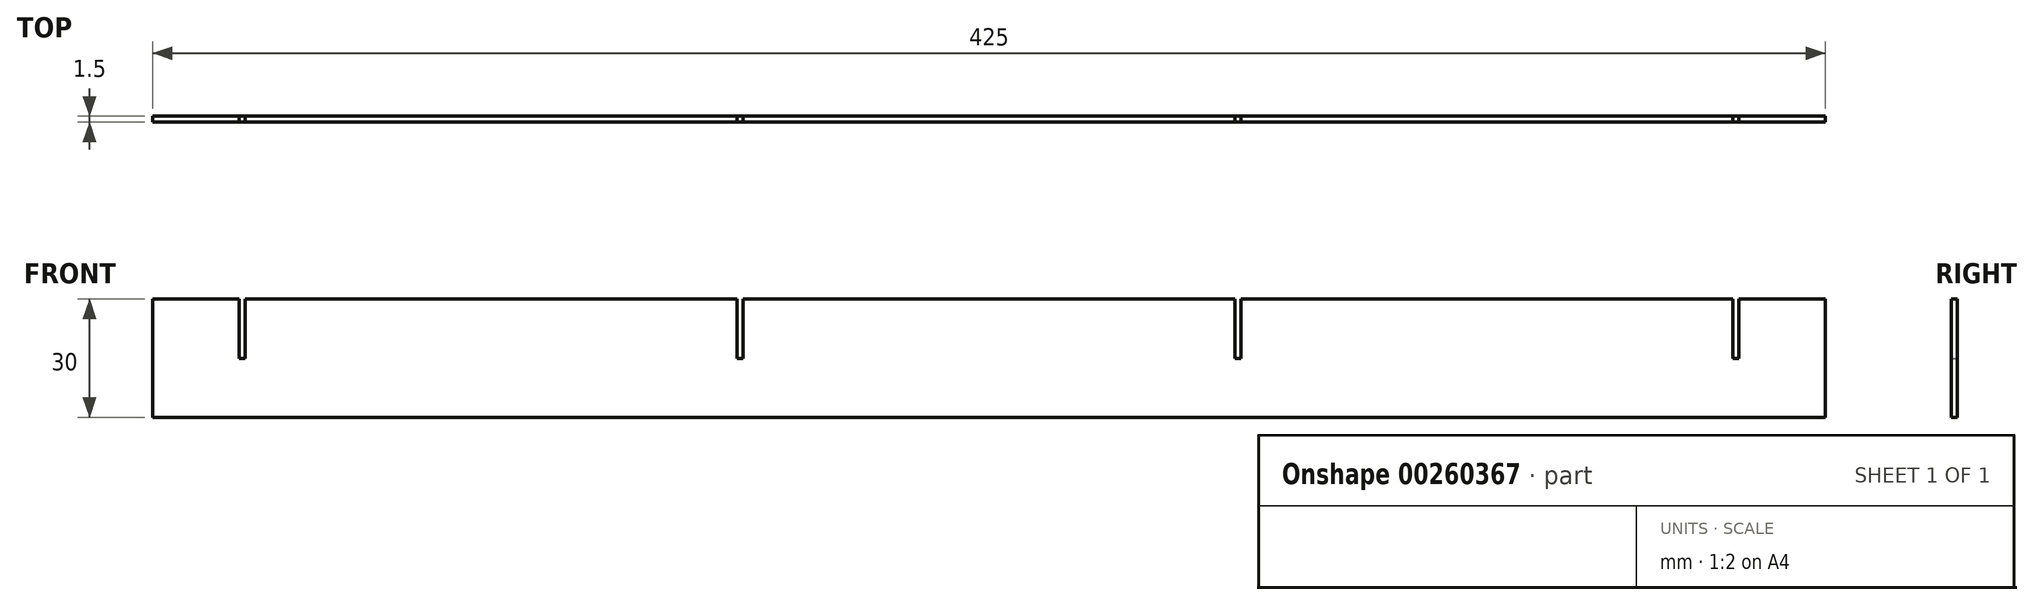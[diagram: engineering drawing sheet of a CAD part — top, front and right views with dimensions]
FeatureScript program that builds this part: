
annotation { "Feature Type Name" : "Feature", "Feature Type Description" : "" }
export const myFeature = defineFeature(function(context is Context, id is Id, definition is map)
    precondition{}
    {
        {
            var Q0;
            Q0=qCreatedBy(makeId("Front.planeOp"),FACE);
            var sketch = newSketch(context, id + "F0", { "sketchPlane" : qUnion([Q0])});
            skLineSegment(sketch, "E0.bottom", {"start": v(212.5, 15) * mm, "end": v(190.5, 15) * mm});
            skLineSegment(sketch, "E0.top", {"start": v(212.5, -15) * mm, "end": v(-212.5, -15) * mm});
            skLineSegment(sketch, "E0.left", {"start": v(212.5, 15) * mm, "end": v(212.5, -15) * mm});
            skLineSegment(sketch, "E0.right", {"start": v(-212.5, 15) * mm, "end": v(-212.5, -15) * mm});
            skPoint(sketch, "E0.middle", {"position": v(0, 0) * mm});
            skLineSegment(sketch, "E1", {"start": v(-190.5, 15) * mm, "end": v(-190.5, 0) * mm});
            skLineSegment(sketch, "E2", {"start": v(-190.5, 0) * mm, "end": v(-189, 0) * mm});
            skLineSegment(sketch, "E3", {"start": v(-189, 0) * mm, "end": v(-189, 15) * mm});
            skLineSegment(sketch, "E4", {"start": v(-64, 15) * mm, "end": v(-64, 0) * mm});
            skLineSegment(sketch, "E5", {"start": v(-64, 0) * mm, "end": v(-62.5, 0) * mm});
            skLineSegment(sketch, "E6", {"start": v(-62.5, 0) * mm, "end": v(-62.5, 15) * mm});
            skLineSegment(sketch, "E7.MirrorCS", {"start": v(190.5, 0) * mm, "end": v(189, 0) * mm});
            skLineSegment(sketch, "E8.MirrorCS", {"start": v(64, 0) * mm, "end": v(62.5, 0) * mm});
            skLineSegment(sketch, "E9.MirrorCS", {"start": v(62.5, 0) * mm, "end": v(62.5, 15) * mm});
            skLineSegment(sketch, "E10.MirrorCS", {"start": v(64, 15) * mm, "end": v(64, 0) * mm});
            skLineSegment(sketch, "E11.MirrorCS", {"start": v(-212.5, 15) * mm, "end": v(-190.5, 15) * mm});
            skLineSegment(sketch, "E12.MirrorCS", {"start": v(190.5, 15) * mm, "end": v(190.5, 0) * mm});
            skLineSegment(sketch, "E13.MirrorCS", {"start": v(189, 0) * mm, "end": v(189, 15) * mm});
            skLineSegment(sketch, "E14.trimOffspring", {"start": v(-190.5, 15) * mm, "end": v(-212.5, 15) * mm});
            skLineSegment(sketch, "E15.trimOffspring", {"start": v(-189, 15) * mm, "end": v(-64, 15) * mm});
            skLineSegment(sketch, "E16.trimOffspring", {"start": v(-62.5, 15) * mm, "end": v(62.5, 15) * mm});
            skLineSegment(sketch, "E17.trimOffspring", {"start": v(-64, 15) * mm, "end": v(-189, 15) * mm});
            skLineSegment(sketch, "E18.trimOffspring", {"start": v(62.5, 15) * mm, "end": v(-62.5, 15) * mm});
            skLineSegment(sketch, "E19.trimOffspring", {"start": v(64, 15) * mm, "end": v(189, 15) * mm});
            skLineSegment(sketch, "E20.trimOffspring", {"start": v(190.5, 15) * mm, "end": v(212.5, 15) * mm});
            skLineSegment(sketch, "E21.trimOffspring", {"start": v(189, 15) * mm, "end": v(64, 15) * mm});
            skSolve(sketch);
        }
        {
            var Q0;
            Q0 = qSketchRegion(id + "F0", true);
            extrude(context, id + "F1", {"entities" : qUnion([Q0]), "depth" : 1.5 * mm});
        }
    });
